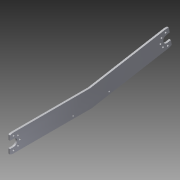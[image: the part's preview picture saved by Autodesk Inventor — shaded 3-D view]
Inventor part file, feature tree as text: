
AUTODESK INVENTOR PART (.ipt)
format: ipt  version: 2013 (Build 170138000, 138)  size: 2,844,672 bytes
history: native  units: mm
features: sketch x10, hole x6, extrude x4, other x2, pattern_circular x2, fillet x1
ambient origin geometry x8: Origin, YZ Plane, XZ Plane, XY Plane, X Axis, Y Axis, Z Axis, Center Point
feature tree (25):
  other  "ソリッド1"
  extrude  "押し出し1"  Depth=20.0mm
  hole  "穴2"  [1 undecoded]
  extrude  "押し出し2"  Depth=10.0mm
  hole  "穴3"  [1 undecoded]
  hole  "穴4"  [1 undecoded]
  pattern_circular  "円形状パターン3"  [2 undecoded]
  hole  "穴5"  [1 undecoded]
  hole  "穴6"  [1 undecoded]
  extrude  "押し出し4"  Depth=4.0mm
  fillet  "フィレット1"  Radius=170.0mm
  extrude  "押し出し5"  Depth=2.0mm TaperAngle=0.0deg
  hole  "穴7"  [1 undecoded]
  pattern_circular  "円形状パターン4"  Count=4  [1 undecoded]
  sketch  "スケッチ2"
  sketch  "スケッチ4"
  sketch  "スケッチ5"
  sketch  "スケッチ6"
  sketch  "スケッチ7"
  sketch  "スケッチ8"
  sketch  "スケッチ11"
  sketch  "スケッチ13"
  sketch  "スケッチ14"
  sketch  "スケッチ15"
  other  "断面エッジを投影1"
note: 9 required parameter values undecoded (feature->parameter linkage not recoverable at this tier; creation-order binding heuristic only, values carry confidence <= 0.55)
